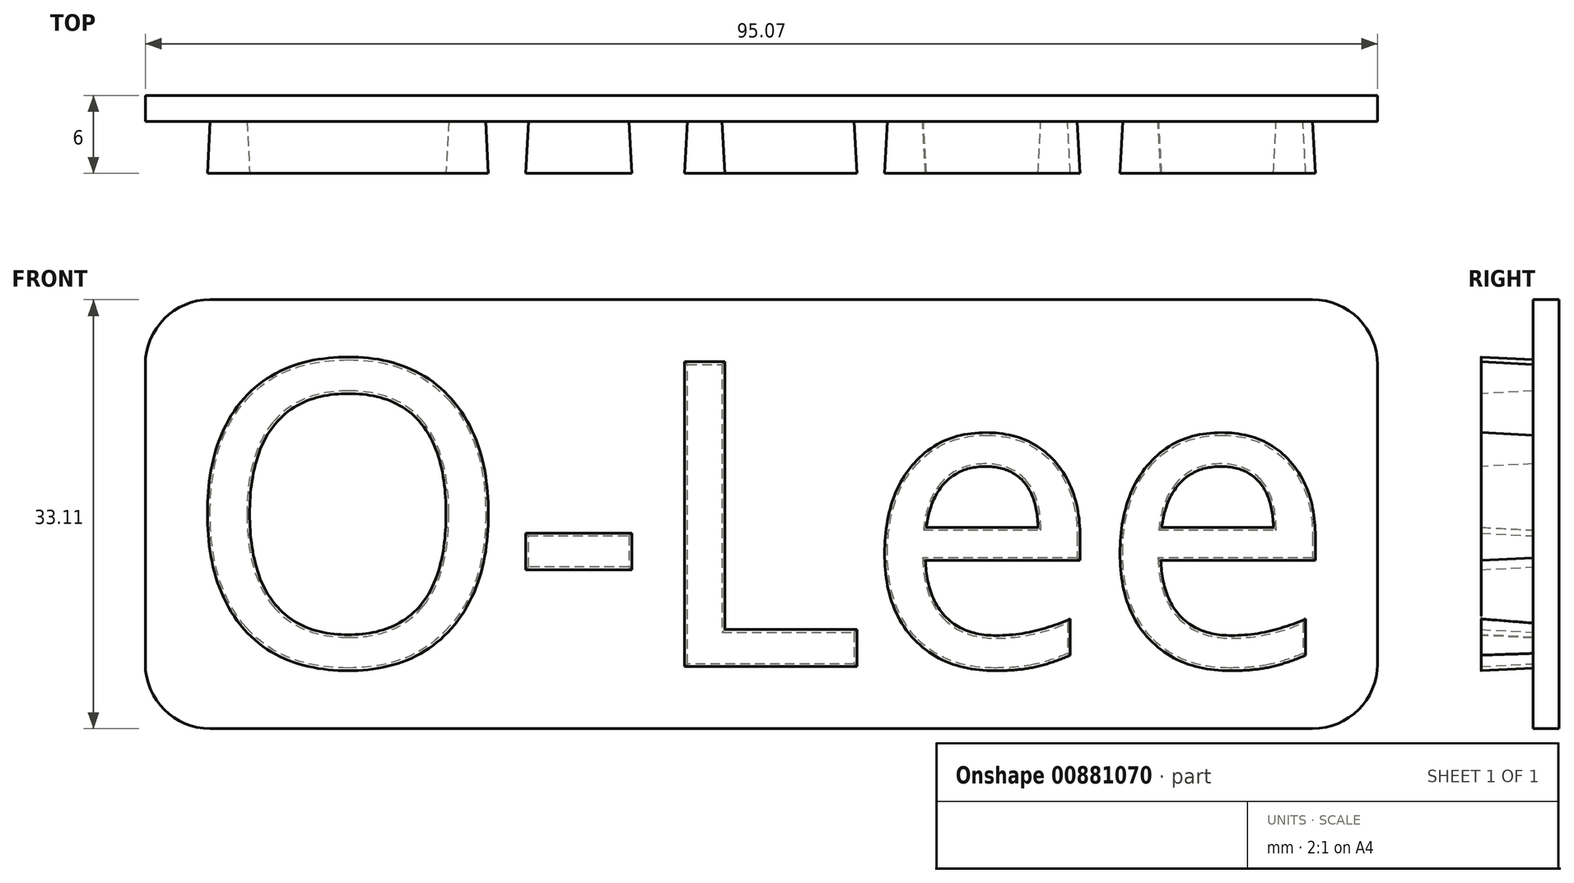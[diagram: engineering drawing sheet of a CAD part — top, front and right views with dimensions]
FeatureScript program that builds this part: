
annotation { "Feature Type Name" : "Feature", "Feature Type Description" : "" }
export const myFeature = defineFeature(function(context is Context, id is Id, definition is map)
    precondition{}
    {
        {
            assignVariable(context, id + "F0", {"name" : "tiefe", "anyValue" : 4 * mm});
        }
        {
            var Q0;
            Q0=qCreatedBy(makeId("Front.planeOp"),FACE);
            var sketch = newSketch(context, id + "F1", { "sketchPlane" : qUnion([Q0])});
            skText(sketch, "E0", { "text": "O-Lee", "fontName": "OpenSans-Regular.ttf"});
            const initialGuessF1  = {"E0": [-0.03607, 0, 1, 0, 0.0233]};
            skSetInitialGuess(sketch, initialGuessF1);
            skSolve(sketch);
        }
        {
            var Q0;
            Q0 = qSketchRegion(id + "F1", true);
            extrude(context, id + "F2", {"entities" : qUnion([Q0]), "depth" : getVariable(context, 'tiefe'), "offsetDistance" : 25 * mm, "hasDraft" : true, "draftAngle" : 3 * degree});
        }
        {
            var Q0;
            Q0=qCreatedBy(makeId("Front.planeOp"),FACE);
            var sketch = newSketch(context, id + "F3", { "sketchPlane" : qUnion([Q0])});
            skLineSegment(sketch, "E1.bottom", {"start": v(55.97, 28.1) * mm, "end": v(-39.1, 28.1) * mm});
            skLineSegment(sketch, "E1.top", {"start": v(55.97, -5) * mm, "end": v(-39.1, -5) * mm});
            skLineSegment(sketch, "E1.left", {"start": v(55.97, 28.1) * mm, "end": v(55.97, -5) * mm});
            skLineSegment(sketch, "E1.right", {"start": v(-39.1, 28.1) * mm, "end": v(-39.1, -5) * mm});
            skSolve(sketch);
        }
        {
            assignVariable(context, id + "F4", {"name" : "tiefe", "anyValue" : 2});
        }
        {
            var Q0;
            Q0=makeQuery(id+"F3.imprint","IMPRINT",FACE,{"disambiguationData":[TD([[makeQuery(id+"F3.imprint","IMPRINT",EDGE,{"derivedFrom":sQuery(id+"F3.wireOp",EDGE,"E1.bottom")}),1.0]])]});
            extrude(context, id + "F5", {"entities" : qUnion([Q0]), "oppositeDirection" : true, "depth" : getVariable(context, 'tiefe') * mm, "offsetDistance" : 25 * mm});
        }
        {
            var Q0;
            Q0=makeQuery(id+"F5.opExtrude","SWEPT_EDGE",EDGE,{"disambiguationData":[OSD([sQuery(id+"F3.wireOp",EDGE,"E1.bottom"),sQuery(id+"F3.wireOp",EDGE,"E1.left")])]});
            var Q1;
            Q1=makeQuery(id+"F5.opExtrude","SWEPT_EDGE",EDGE,{"disambiguationData":[OSD([sQuery(id+"F3.wireOp",EDGE,"E1.top"),sQuery(id+"F3.wireOp",EDGE,"E1.left")])]});
            var Q2;
            Q2=makeQuery(id+"F5.opExtrude","SWEPT_EDGE",EDGE,{"disambiguationData":[OSD([sQuery(id+"F3.wireOp",EDGE,"E1.bottom"),sQuery(id+"F3.wireOp",EDGE,"E1.right")])]});
            var Q3;
            Q3=makeQuery(id+"F5.opExtrude","SWEPT_EDGE",EDGE,{"disambiguationData":[OSD([sQuery(id+"F3.wireOp",EDGE,"E1.top"),sQuery(id+"F3.wireOp",EDGE,"E1.right")])]});
            fillet(context, id + "F6", {"entities" : qUnion([Q0, Q1, Q2, Q3]), "radius" : 5 * mm, "tangentPropagation" : true, "allowEdgeOverflow" : false});
        }
    });
